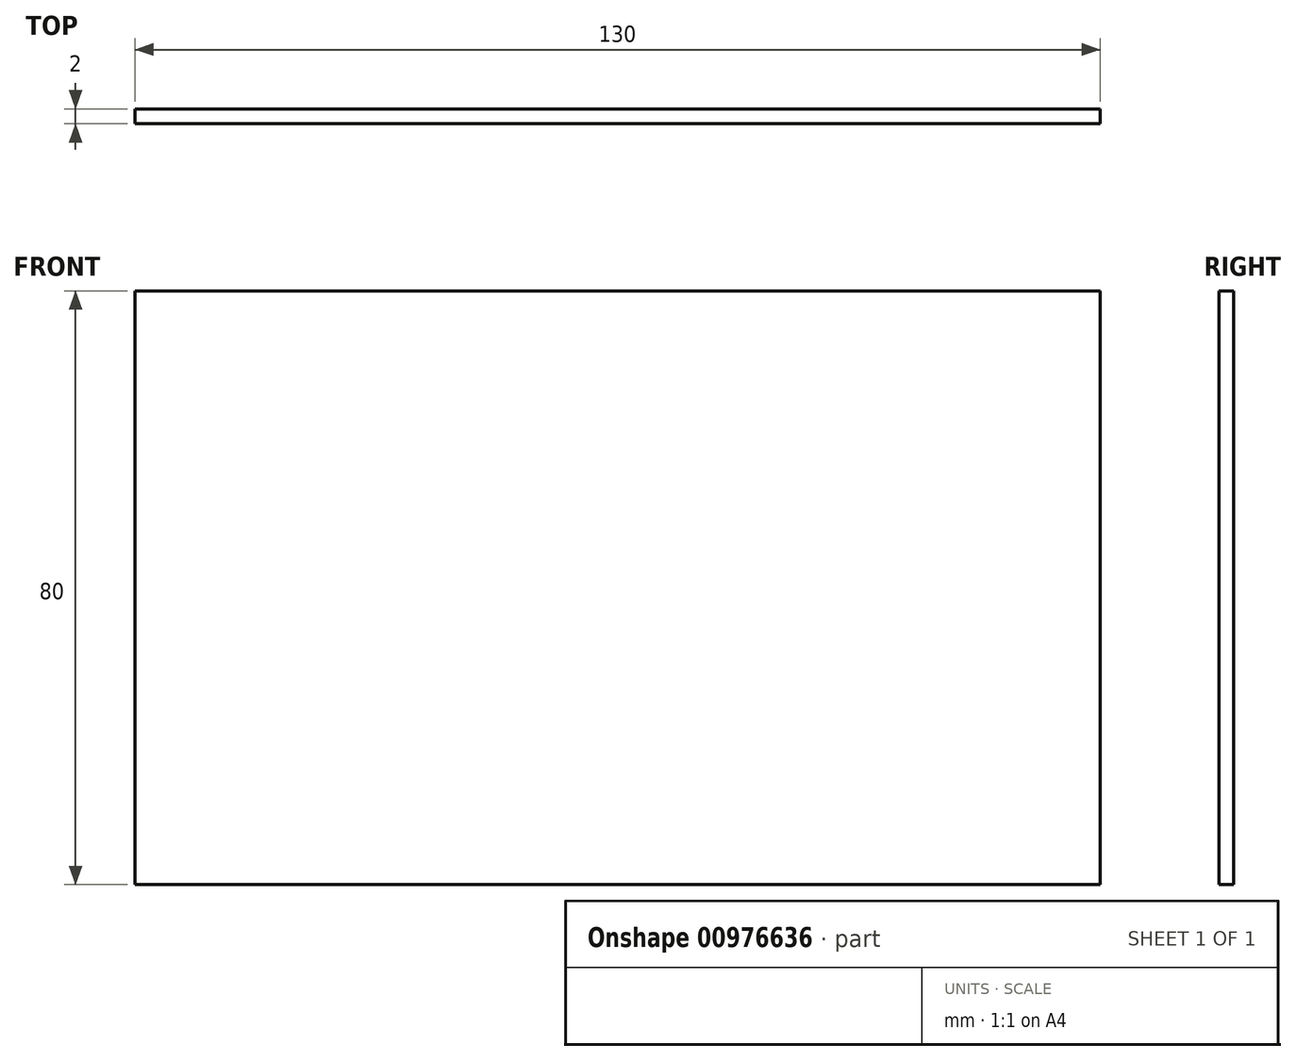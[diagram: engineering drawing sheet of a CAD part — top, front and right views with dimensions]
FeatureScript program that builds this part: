
annotation { "Feature Type Name" : "Feature", "Feature Type Description" : "" }
export const myFeature = defineFeature(function(context is Context, id is Id, definition is map)
    precondition{}
    {
        {
            var Q0;
            Q0=qCreatedBy(makeId("Front.planeOp"),FACE);
            var sketch = newSketch(context, id + "F0", { "sketchPlane" : qUnion([Q0])});
            skLineSegment(sketch, "E0.bottom", {"start": v(-65, -40) * mm, "end": v(65, -40) * mm});
            skLineSegment(sketch, "E0.top", {"start": v(-65, 40) * mm, "end": v(65, 40) * mm});
            skLineSegment(sketch, "E0.left", {"start": v(-65, -40) * mm, "end": v(-65, 40) * mm});
            skLineSegment(sketch, "E0.right", {"start": v(65, -40) * mm, "end": v(65, 40) * mm});
            skPoint(sketch, "E0.middle", {"position": v(0, 0) * mm});
            skSolve(sketch);
        }
        {
            var Q0;
            Q0=makeQuery(id+"F0.imprint","IMPRINT",FACE,{"disambiguationData":[TD([[makeQuery(id+"F0.imprint","IMPRINT",EDGE,{"derivedFrom":sQuery(id+"F0.wireOp",EDGE,"E0.bottom")}),1.0]])]});
            extrude(context, id + "F1", {"entities" : qUnion([Q0]), "depth" : 2 * mm, "offsetDistance" : 25 * mm});
        }
    });
